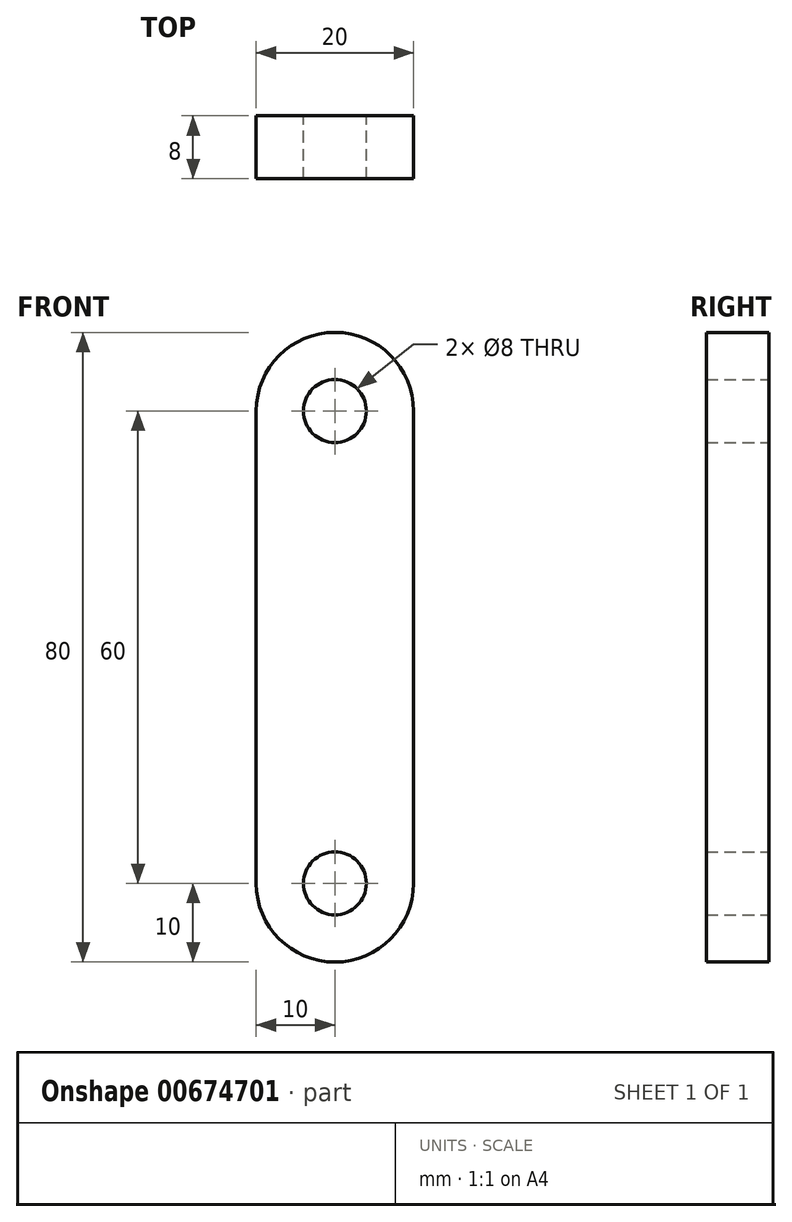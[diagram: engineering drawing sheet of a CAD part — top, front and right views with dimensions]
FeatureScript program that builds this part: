
annotation { "Feature Type Name" : "Feature", "Feature Type Description" : "" }
export const myFeature = defineFeature(function(context is Context, id is Id, definition is map)
    precondition{}
    {
        {
            var Q0;
            Q0=qCreatedBy(makeId("Front.planeOp"),FACE);
            var sketch = newSketch(context, id + "F0", { "sketchPlane" : qUnion([Q0])});
            skCircle(sketch, "E0", {"center": v(0, 0) * mm, "radius": 10 * mm});
            skCircle(sketch, "E1", {"center": v(0, 60) * mm, "radius": 10 * mm});
            skCircle(sketch, "E2", {"center": v(0, 60) * mm, "radius": 4 * mm});
            skCircle(sketch, "E3", {"center": v(0, 0) * mm, "radius": 4 * mm});
            skLineSegment(sketch, "E4", {"start": v(-10, 60) * mm, "end": v(-10, 0) * mm});
            skLineSegment(sketch, "E5", {"start": v(10, 60) * mm, "end": v(10, 0) * mm});
            skSolve(sketch);
        }
        {
            var Q0;
            Q0 = qSketchRegion(id + "F0", true);
            extrude(context, id + "F1", {"entities" : qUnion([Q0]), "depth" : 8 * mm, "offsetDistance" : 25 * mm});
        }
    });
